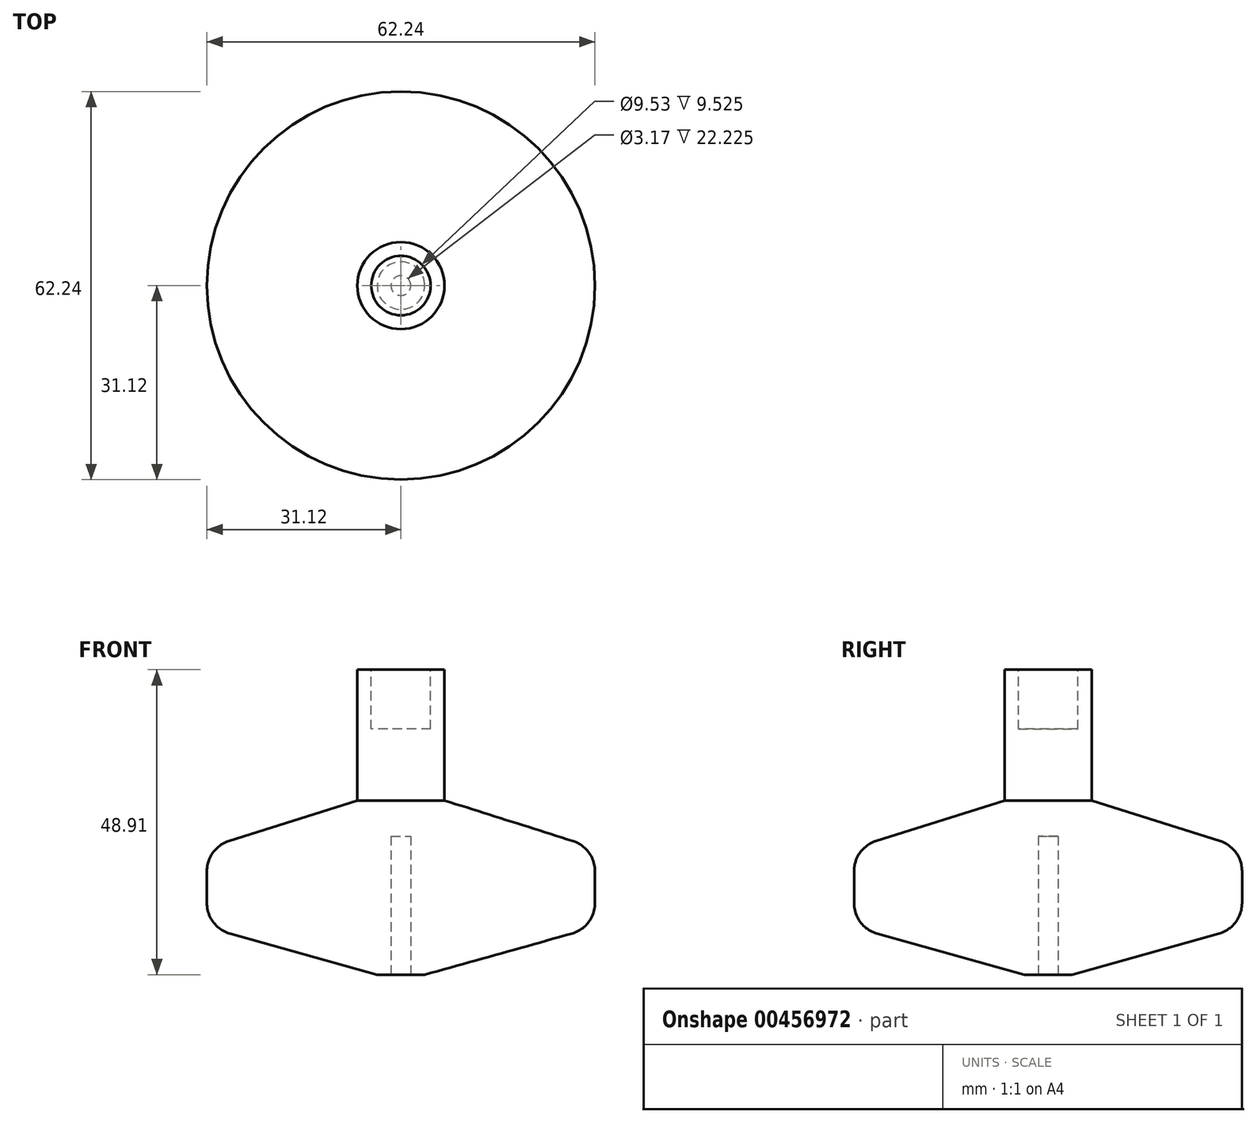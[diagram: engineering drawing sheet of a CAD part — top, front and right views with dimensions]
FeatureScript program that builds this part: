
annotation { "Feature Type Name" : "Feature", "Feature Type Description" : "" }
export const myFeature = defineFeature(function(context is Context, id is Id, definition is map)
    precondition{}
    {
        {
            var Q0;
            Q0=qCreatedBy(makeId("Front.planeOp"),FACE);
            var sketch = newSketch(context, id + "F0", { "sketchPlane" : qUnion([Q0])});
            skLineSegment(sketch, "E0", {"start": v(31.12, 9.5) * mm, "end": v(31.12, 22.2) * mm});
            skLineSegment(sketch, "E1", {"start": v(6.99, 50.8) * mm, "end": v(0, 50.8) * mm});
            skLineSegment(sketch, "E2", {"start": v(0, 50.8) * mm, "end": v(0, 1.89) * mm});
            skLineSegment(sketch, "E3", {"start": v(0, 1.89) * mm, "end": v(3.81, 1.89) * mm});
            skLineSegment(sketch, "E4", {"start": v(3.81, 1.89) * mm, "end": v(31.12, 9.5) * mm});
            skLineSegment(sketch, "E5", {"start": v(31.12, 22.2) * mm, "end": v(6.99, 29.83) * mm});
            skLineSegment(sketch, "E6", {"start": v(6.99, 29.83) * mm, "end": v(6.99, 50.8) * mm});
            skSolve(sketch);
        }
        {
            var Q0;
            Q0=makeQuery(id+"F0.imprint","IMPRINT",FACE,{"disambiguationData":[TD([[makeQuery(id+"F0.imprint","IMPRINT",EDGE,{"derivedFrom":sQuery(id+"F0.wireOp",EDGE,"E0")}),1.0]])]});
            var Q1;
            Q1=sQuery(id+"F0.wireOp",EDGE,"E2");
            revolve(context, id + "F1", {"entities" : qUnion([Q0]), "axis" : qUnion([Q1]), "revolveType" : RevolveType.FULL});
        }
        {
            var Q0;
            Q0=makeQuery(id+"F1.opRevolve","SWEPT_FACE",FACE,{"disambiguationData":[OSD([sQuery(id+"F0.wireOp",EDGE,"E1")])]});
            var sketch = newSketch(context, id + "F2", { "sketchPlane" : qUnion([Q0])});
            skCircle(sketch, "E7", {"center": v(0, 0) * mm, "radius": 4.76 * mm});
            skSolve(sketch);
        }
        {
            var Q0;
            Q0=makeQuery(id+"F2.imprint","IMPRINT",FACE,{"disambiguationData":[TD([[makeQuery(id+"F2.imprint","IMPRINT",EDGE,{"derivedFrom":sQuery(id+"F2.wireOp",EDGE,"E7")}),1.0]])]});
            extrude(context, id + "F3", {"entities" : qUnion([Q0]), "operationType" : NewBodyOperationType.REMOVE, "oppositeDirection" : true, "depth" : 9.52 * mm});
        }
        {
            var Q0;
            Q0=makeQuery(id+"F1.opRevolve","SWEPT_FACE",FACE,{"disambiguationData":[OSD([sQuery(id+"F0.wireOp",EDGE,"E3")])]});
            var sketch = newSketch(context, id + "F4", { "sketchPlane" : qUnion([Q0])});
            skCircle(sketch, "E8", {"center": v(0, 0) * mm, "radius": 1.59 * mm});
            skSolve(sketch);
        }
        {
            var Q0;
            Q0=qSketchRegion(id+"F4",true);
            extrude(context, id + "F5", {"entities" : qUnion([Q0]), "operationType" : NewBodyOperationType.REMOVE, "oppositeDirection" : true, "depth" : 22.22 * mm});
        }
        {
            var Q0;
            Q0=makeQuery(id+"F1.opRevolve","SWEPT_FACE",FACE,{"disambiguationData":[OSD([sQuery(id+"F0.wireOp",EDGE,"E0")])]});
            fillet(context, id + "F6", {"entities" : qUnion([Q0]), "radius" : 5.08 * mm, "tangentPropagation" : true, "allowEdgeOverflow" : false});
        }
    });
